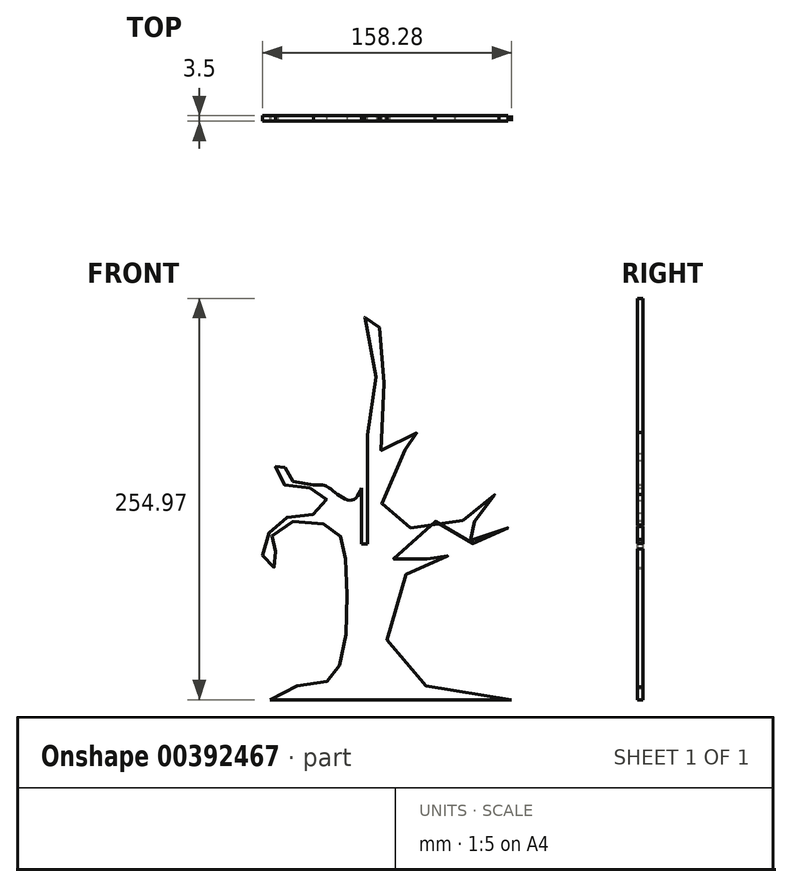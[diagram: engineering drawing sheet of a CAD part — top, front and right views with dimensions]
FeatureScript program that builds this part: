
annotation { "Feature Type Name" : "Feature", "Feature Type Description" : "" }
export const myFeature = defineFeature(function(context is Context, id is Id, definition is map)
    precondition{}
    {
        {
            var Q0;
            Q0=qCreatedBy(makeId("Front.planeOp"),FACE);
            var sketch = newSketch(context, id + "F0", { "sketchPlane" : qUnion([Q0])});
            skLineSegment(sketch, "E0", {"start": v(93.38, 25) * mm, "end": v(-60, 25) * mm});
            skFitSpline(sketch, "E1", {"points": [v(-60, 25) * mm, v(-30.4, 35.08) * mm, v(-18.95, 41.14) * mm, v(-11.9, 64.8) * mm, v(-11.9, 110.62) * mm, v(-15.1, 128.67) * mm, v(-26.7, 136.82) * mm, v(-54, 135.2) * mm, v(-59.41, 122.97) * mm, v(-55.31, 117.11) * mm, v(-57.95, 108.9) * mm, v(-64.4, 115.06) * mm, v(-60.44, 131.42) * mm, v(-46.4, 141.76) * mm, v(-27.18, 144.96) * mm, v(-25.95, 156.79) * mm, v(-45.41, 160) * mm, v(-55.76, 167.14) * mm, v(-55.02, 176.74) * mm, v(-47.88, 167.63) * mm, v(-45.41, 163.69) * mm, v(-32.36, 161.47) * mm], "startDerivative": vector(59.6, 426.15) * mm, "endDerivative": vector(357.05, 20.73) * mm});
            skFitSpline(sketch, "E2", {"points": [v(-32.36, 161.47) * mm, v(-21.76, 159) * mm, v(-7.85, 151.82) * mm, v(0, 167.14) * mm, v(1.88, 182.67) * mm, v(2.25, 210.18) * mm, v(4.4, 220.71) * mm, v(8.77, 246.92) * mm, v(0, 261.97) * mm, v(6.19, 279.97) * mm, v(9.8, 267.12) * mm, v(9.27, 255.78) * mm, v(14.17, 236.16) * mm, v(8.92, 213.91) * mm, v(9.77, 185.12) * mm, v(13.96, 181.42) * mm, v(28, 188.32) * mm, v(33.16, 194.4) * mm, v(44.5, 193.09) * mm, v(34.16, 187.58) * mm, v(12.23, 173.05) * mm, v(11.04, 153.05) * mm, v(13.83, 126.5) * mm, v(32.64, 136.88) * mm, v(48.1, 143.4) * mm, v(64, 138.63) * mm, v(71.76, 143.22) * mm, v(75.84, 150.68) * mm, v(84.8, 155.15) * mm, v(81.63, 146.2) * mm, v(73.62, 140.8) * mm, v(63.2, 135.77) * mm, v(57.6, 135.77) * mm, v(64.3, 127.2) * mm, v(76.98, 128.69) * mm, v(80.14, 132.79) * mm, v(90.85, 134.34) * mm, v(85.58, 127.5) * mm, v(78.1, 126.82) * mm, v(67.3, 124.22) * mm, v(54.74, 133.1) * mm, v(49.04, 138.37) * mm, v(38.8, 135.58) * mm, v(27.99, 123.84) * mm, v(16.22, 110.5) * mm, v(26.88, 108.93) * mm, v(39.9, 114.72) * mm, v(45.54, 120.38) * mm, v(57.66, 119.06) * mm, v(48.97, 115.38) * mm, v(43.42, 114.27) * mm, v(31.07, 106.09) * mm, v(17.56, 100) * mm, v(14.41, 60.57) * mm, v(21.15, 42.4) * mm, v(54.55, 32.15) * mm, v(93.38, 25) * mm], "startDerivative": vector(1262.36, 52.6) * mm, "endDerivative": vector(318.33, -1246.54) * mm});
            skSolve(sketch);
        }
        {
            var Q0;
            Q0=qSketchRegion(id+"F0",true);
            extrude(context, id + "F1", {"entities" : qUnion([Q0]), "depth" : 3.5 * mm});
        }
        {
            var Q0;
            Q0=qCreatedBy(makeId("Front.planeOp"),FACE);
            var sketch = newSketch(context, id + "F2", { "sketchPlane" : qUnion([Q0])});
            skLineSegment(sketch, "E3.bottom", {"start": v(2, 250) * mm, "end": v(-2, 250) * mm});
            skLineSegment(sketch, "E3.top", {"start": v(2, 124) * mm, "end": v(-2, 124) * mm});
            skLineSegment(sketch, "E3.left", {"start": v(2, 250) * mm, "end": v(2, 124) * mm});
            skLineSegment(sketch, "E3.right", {"start": v(-2, 250) * mm, "end": v(-2, 124) * mm});
            skSolve(sketch);
        }
        {
            var Q0;
            Q0=qSketchRegion(id+"F2",true);
            extrude(context, id + "F3", {"entities" : qUnion([Q0]), "operationType" : NewBodyOperationType.REMOVE, "depth" : 25 * mm});
        }
    });
